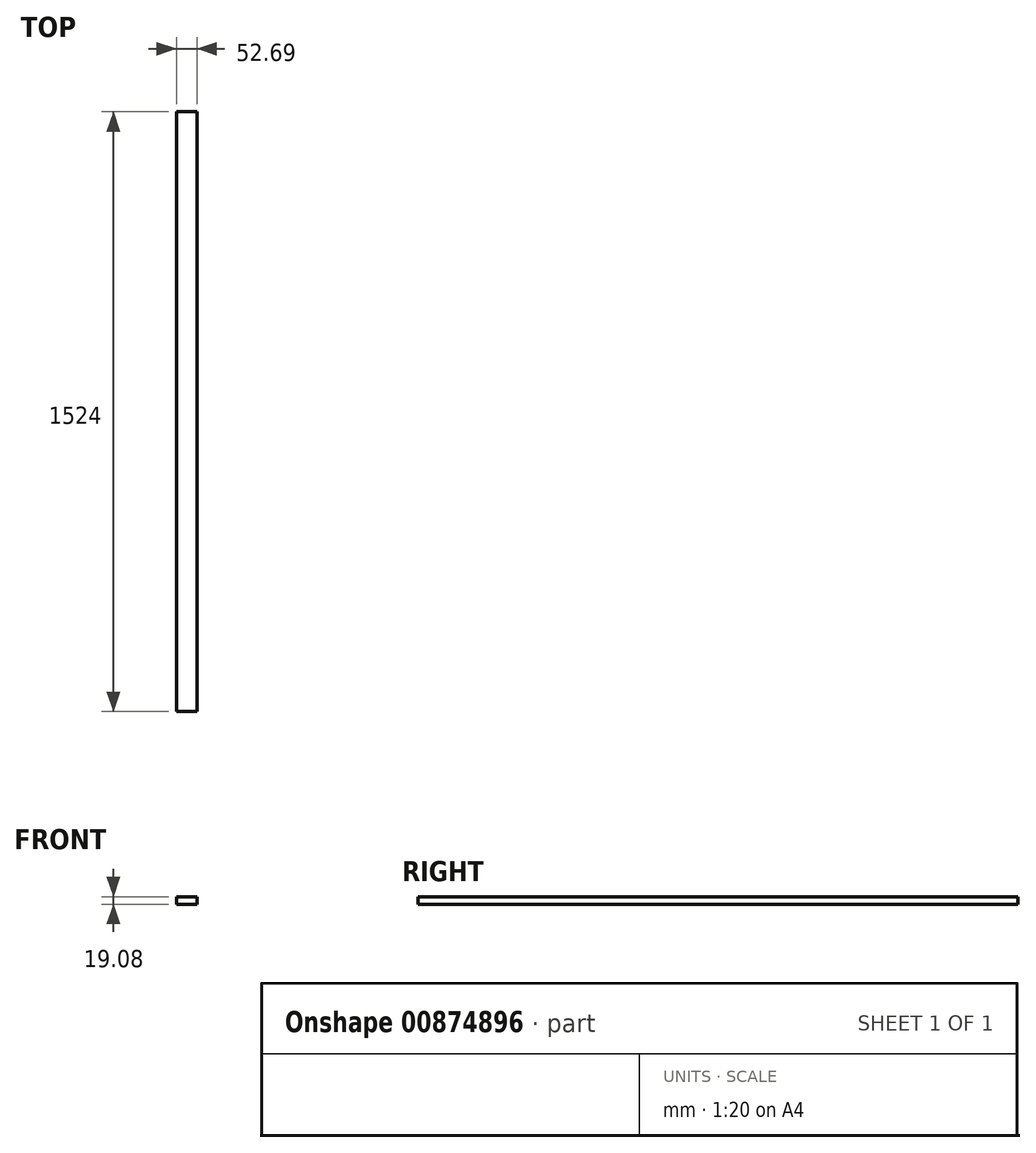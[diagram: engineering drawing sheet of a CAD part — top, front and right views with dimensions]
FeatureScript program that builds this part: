
annotation { "Feature Type Name" : "Feature", "Feature Type Description" : "" }
export const myFeature = defineFeature(function(context is Context, id is Id, definition is map)
    precondition{}
    {
        {
            var Q0;
            Q0=qCreatedBy(makeId("Front.planeOp"),FACE);
            var sketch = newSketch(context, id + "F0", { "sketchPlane" : qUnion([Q0])});
            skLineSegment(sketch, "E0", {"start": v(-46, 37.88) * mm, "end": v(-46, 18.8) * mm});
            skLineSegment(sketch, "E1", {"start": v(-46, 18.8) * mm, "end": v(6.7, 18.8) * mm});
            skLineSegment(sketch, "E2", {"start": v(6.7, 18.8) * mm, "end": v(6.7, 37.88) * mm});
            skLineSegment(sketch, "E3", {"start": v(6.7, 37.88) * mm, "end": v(-46, 37.88) * mm});
            skSolve(sketch);
        }
        {
            var Q0;
            Q0 = qSketchRegion(id + "F0", true);
            extrude(context, id + "F1", {"entities" : qUnion([Q0]), "depth" : 1524 * mm, "offsetDistance" : 25.4 * mm});
        }
    });
